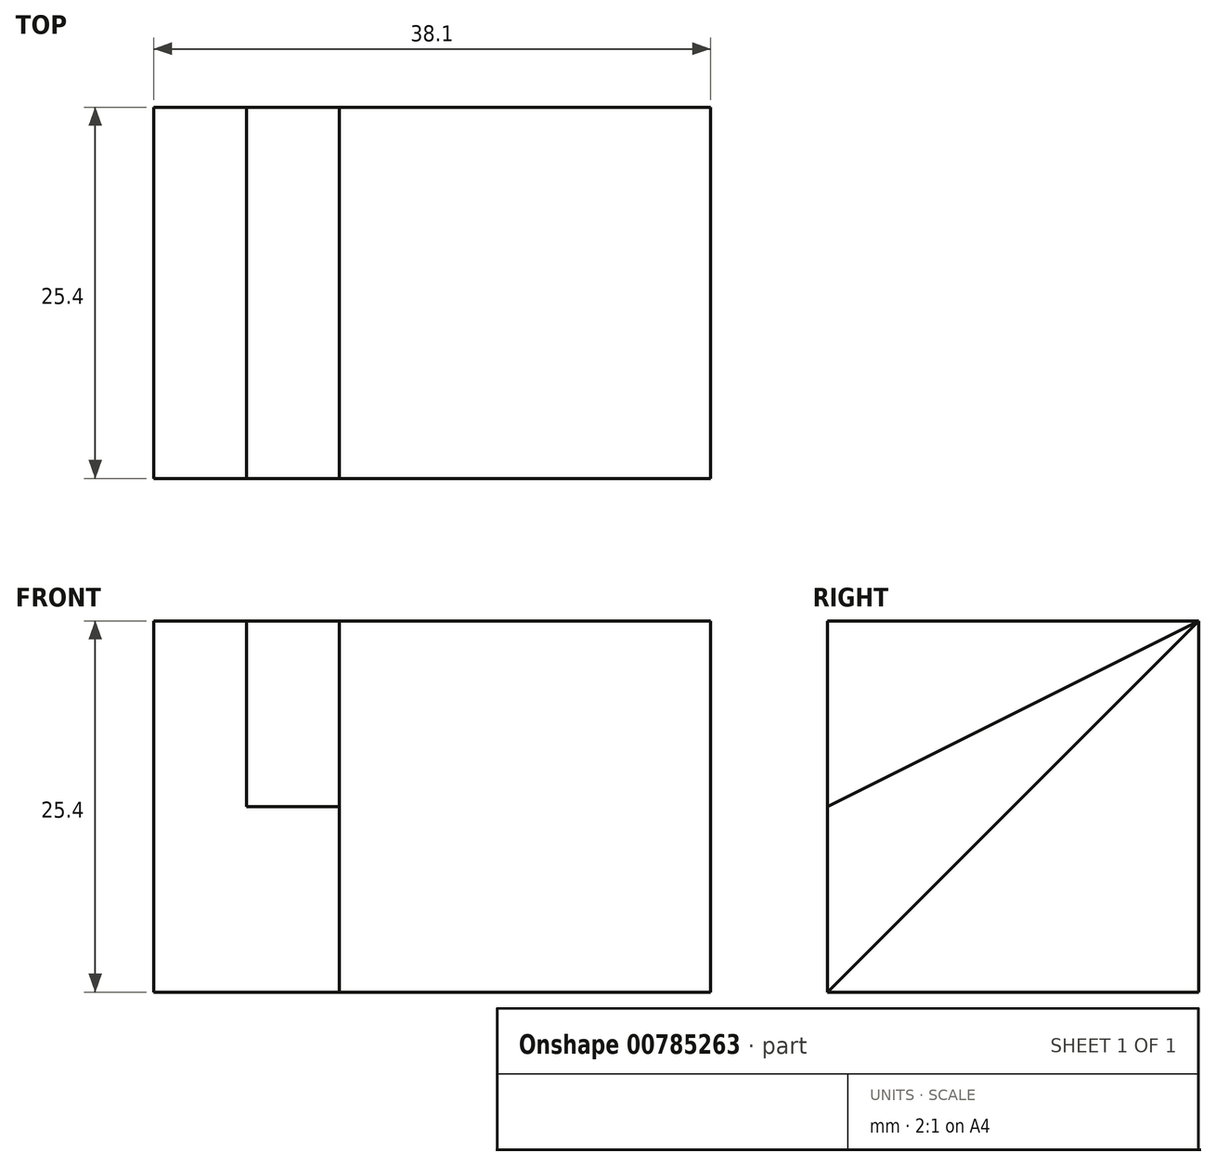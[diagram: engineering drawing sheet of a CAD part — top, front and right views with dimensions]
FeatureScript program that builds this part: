
annotation { "Feature Type Name" : "Feature", "Feature Type Description" : "" }
export const myFeature = defineFeature(function(context is Context, id is Id, definition is map)
    precondition{}
    {
        {
            var Q0;
            Q0=qCreatedBy(makeId("Right.planeOp"),FACE);
            var sketch = newSketch(context, id + "F0", { "sketchPlane" : qUnion([Q0])});
            skLineSegment(sketch, "E0", {"start": v(0, 0) * mm, "end": v(-25.4, 0) * mm});
            skLineSegment(sketch, "E1", {"start": v(-25.4, 0) * mm, "end": v(-25.4, 25.4) * mm});
            skLineSegment(sketch, "E2", {"start": v(-25.4, 25.4) * mm, "end": v(0, 25.4) * mm});
            skLineSegment(sketch, "E3", {"start": v(0, 25.4) * mm, "end": v(0, 0) * mm});
            skSolve(sketch);
        }
        {
            var Q0;
            Q0 = qSketchRegion(id + "F0", true);
            extrude(context, id + "F1", {"entities" : qUnion([Q0]), "oppositeDirection" : true, "depth" : 38.1 * mm, "offsetDistance" : 25.4 * mm});
        }
        {
            var Q0;
            Q0=makeQuery(id+"F1.opExtrude","CAP_FACE",FACE,{"disambiguationData":[OSD([sQuery(id+"F0.wireOp",EDGE,"E0"),sQuery(id+"F0.wireOp",EDGE,"E1"),sQuery(id+"F0.wireOp",EDGE,"E2"),sQuery(id+"F0.wireOp",EDGE,"E3")])],"isStart":true});
            var sketch = newSketch(context, id + "F2", { "sketchPlane" : qUnion([Q0])});
            skLineSegment(sketch, "E4", {"start": v(0, 0) * mm, "end": v(0, 25.4) * mm});
            skLineSegment(sketch, "E5", {"start": v(0, 0) * mm, "end": v(-25.4, 0) * mm});
            skLineSegment(sketch, "E6", {"start": v(-25.4, 0) * mm, "end": v(0, 25.4) * mm});
            skSolve(sketch);
        }
        {
            var Q0;
            Q0=makeQuery(id+"F2.imprint","IMPRINT",FACE,{"disambiguationData":[TD([[makeQuery(id+"F2.imprint","IMPRINT",EDGE,{"derivedFrom":sQuery(id+"F2.wireOp",EDGE,"E6")}),1.0]])]});
            var sketch = newSketch(context, id + "F3", { "sketchPlane" : qUnion([Q0])});
            skSolve(sketch);
        }
        {
            var Q0;
            Q0 = qSketchRegion(id + "F3", true);
            var Q1;
            Q1=makeQuery(id+"F3.imprint","IMPRINT",FACE,{"disambiguationData":[TD([[makeQuery(id+"F3.imprint","IMPRINT",EDGE,{"derivedFrom":makeQuery(id+"F2.imprint","IMPRINT",EDGE,{"derivedFrom":sQuery(id+"F2.wireOp",EDGE,"E6")})}),1.0]])]});
            extrude(context, id + "F4", {"entities" : qUnion([Q0, Q1]), "operationType" : NewBodyOperationType.REMOVE, "oppositeDirection" : true, "depth" : 25.4 * mm, "offsetDistance" : 25.4 * mm});
        }
        {
            var Q0;
            Q0=makeQuery(id+"F4.boolean.opBoolean","COPY",FACE,{"derivedFrom":makeQuery(id+"F4.opExtrude","CAP_FACE",FACE,{"disambiguationData":[OSD([sQuery(id+"F0.wireOp",EDGE,"E1"),sQuery(id+"F0.wireOp",EDGE,"E2"),sQuery(id+"F2.wireOp",EDGE,"E6")])],"isStart":false})});
            var sketch = newSketch(context, id + "F5", { "sketchPlane" : qUnion([Q0])});
            skLineSegment(sketch, "E7", {"start": v(-25.4, 12.7) * mm, "end": v(0, 25.4) * mm});
            skLineSegment(sketch, "E8", {"start": v(-25.4, 12.7) * mm, "end": v(-25.4, 25.4) * mm});
            skLineSegment(sketch, "E9", {"start": v(-25.4, 25.4) * mm, "end": v(0, 25.4) * mm});
            skSolve(sketch);
        }
        {
            var Q0;
            Q0=makeQuery(id+"F5.imprint","IMPRINT",FACE,{"disambiguationData":[TD([[makeQuery(id+"F5.imprint","IMPRINT",EDGE,{"derivedFrom":sQuery(id+"F5.wireOp",EDGE,"E7")}),1.0]])]});
            extrude(context, id + "F6", {"entities" : qUnion([Q0]), "operationType" : NewBodyOperationType.REMOVE, "oppositeDirection" : true, "depth" : 6.35 * mm, "offsetDistance" : 25.4 * mm});
        }
    });
